# Revit family: Showerhead-DXV-Contemporary_D3570141X_Series
name_source: partatom
category: Plumbing Fixtures
revit_build: Autodesk Revit 2014 (Build: 20130308_1515(x64)
units: mm (PartAtom-declared; Revit-internal decimal feet)

## types (2) — shared parameters
Assembly Code = D2010710
CW Connection = Yes
CWFU = 3
Default Elevation = 0"
Finish = Brass-DXV-100-Polished Chrome
Flow Rate = 2.5 gpm.  (9.5 L/min.)
HW Connection = Yes
HWFU = 3
Manufacturer = DXV
Material = Brass-DXV-100-Polished Chrome
Price = Prices may vary. Please consult Manufacturer Representative for most up-to-date price list.
Product Documentation Link = https://dxv01.blob.core.windows.net
Product Page URL = https://www.dxv.com
URL = https://www.dxv.com
Vent Connection = No
WFU = 4
Warranty Documentation Link = https://www.dxv.com
Waste Connection = Yes
Water Connection Diameter = 1/2"

## per-type parameters (varying)
| type | Description | Length |
| D35701410.100 | Slim Round 10 Inch Showerhead Contemporary Accents Collection | 9 7/8" |
| D35701418.100 | Slim Round 8 Inch Showerhead Contemporary Accents Collection | 7 7/8" |

note: column(s) folded — value = type name in every type: Model

## geometry (parser evidence)
native form markers: Sweep x1
no freeform markers — native parametric forms only
